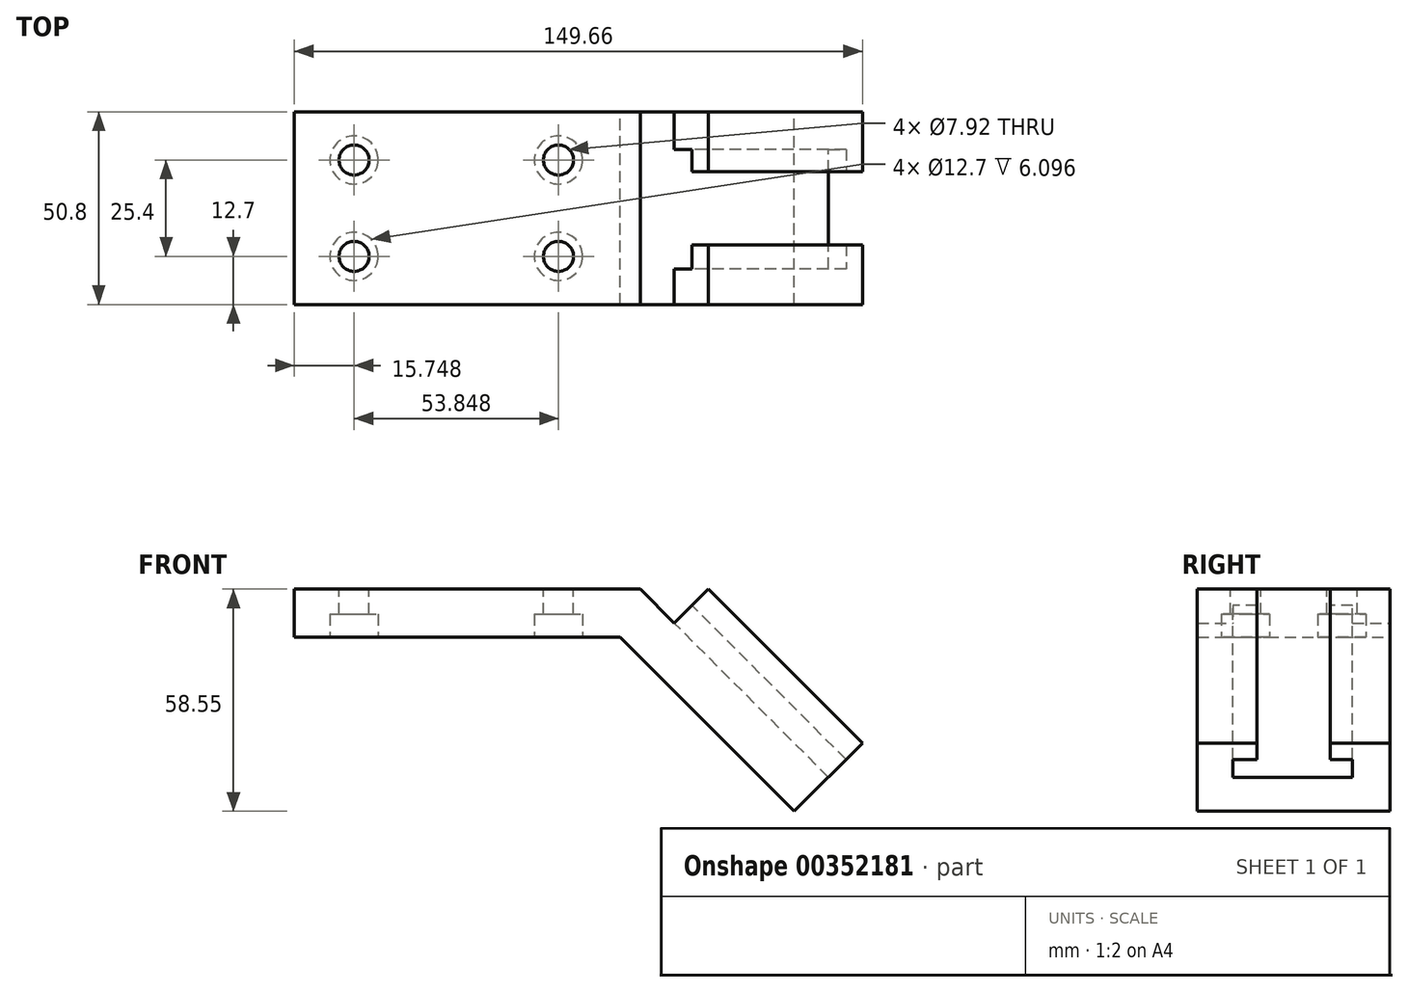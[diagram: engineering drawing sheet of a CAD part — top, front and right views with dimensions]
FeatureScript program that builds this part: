
annotation { "Feature Type Name" : "Feature", "Feature Type Description" : "" }
export const myFeature = defineFeature(function(context is Context, id is Id, definition is map)
    precondition{}
    {
        {
            var Q0;
            Q0=qCreatedBy(makeId("Front.planeOp"),FACE);
            var sketch = newSketch(context, id + "F0", { "sketchPlane" : qUnion([Q0])});
            skLineSegment(sketch, "E0", {"start": v(0, 0) * mm, "end": v(0, -12.7) * mm});
            skLineSegment(sketch, "E1", {"start": v(0, -12.7) * mm, "end": v(85.85, -12.7) * mm});
            skLineSegment(sketch, "E2", {"start": v(0, 0) * mm, "end": v(91.11, 0) * mm});
            skLineSegment(sketch, "E3", {"start": v(91.11, 0) * mm, "end": v(100.1, -8.98) * mm});
            skLineSegment(sketch, "E4", {"start": v(85.85, -12.7) * mm, "end": v(131.7, -58.55) * mm});
            skLineSegment(sketch, "E5", {"start": v(131.7, -58.55) * mm, "end": v(149.66, -40.6) * mm});
            skLineSegment(sketch, "E6", {"start": v(149.66, -40.6) * mm, "end": v(109.07, 0) * mm});
            skLineSegment(sketch, "E7", {"start": v(109.07, 0) * mm, "end": v(100.1, -8.98) * mm});
            skSolve(sketch);
        }
        {
            var Q0;
            Q0 = qSketchRegion(id + "F0", true);
            extrude(context, id + "F1", {"entities" : qUnion([Q0]), "endBound" : BoundingType.SYMMETRIC, "depth" : 50.8 * mm});
        }
        {
            var Q0;
            Q0=makeQuery(id+"F1.opExtrude","SWEPT_FACE",FACE,{"disambiguationData":[OSD([sQuery(id+"F0.wireOp",EDGE,"E2")])]});
            var sketch = newSketch(context, id + "F2", { "sketchPlane" : qUnion([Q0])});
            skCircle(sketch, "E8", {"center": v(15.75, 12.7) * mm, "radius": 3.96 * mm});
            skCircle(sketch, "E9", {"center": v(15.75, -12.7) * mm, "radius": 3.96 * mm});
            skCircle(sketch, "E10", {"center": v(69.6, 12.7) * mm, "radius": 3.96 * mm});
            skCircle(sketch, "E11", {"center": v(69.6, -12.7) * mm, "radius": 3.96 * mm});
            skSolve(sketch);
        }
        {
            var Q0;
            Q0 = qSketchRegion(id + "F2", true);
            extrude(context, id + "F3", {"entities" : qUnion([Q0]), "operationType" : NewBodyOperationType.REMOVE, "endBound" : BoundingType.THROUGH_ALL, "oppositeDirection" : true, "depth" : 25.4 * mm});
        }
        {
            var Q0;
            Q0=makeQuery(id+"F1.opExtrude","SWEPT_FACE",FACE,{"disambiguationData":[OSD([sQuery(id+"F0.wireOp",EDGE,"E1")])]});
            var sketch = newSketch(context, id + "F4", { "sketchPlane" : qUnion([Q0])});
            skCircle(sketch, "E12", {"center": v(15.75, 12.7) * mm, "radius": 6.35 * mm});
            skCircle(sketch, "E13", {"center": v(15.75, -12.7) * mm, "radius": 6.35 * mm});
            skCircle(sketch, "E14", {"center": v(69.6, -12.7) * mm, "radius": 6.35 * mm});
            skCircle(sketch, "E15", {"center": v(69.6, 12.7) * mm, "radius": 6.35 * mm});
            skSolve(sketch);
        }
        {
            var Q0;
            Q0 = qSketchRegion(id + "F4", true);
            extrude(context, id + "F5", {"entities" : qUnion([Q0]), "operationType" : NewBodyOperationType.REMOVE, "oppositeDirection" : true, "depth" : 6.1 * mm});
        }
        {
            var Q0;
            Q0=makeQuery(id+"F1.opExtrude","SWEPT_FACE",FACE,{"disambiguationData":[OSD([sQuery(id+"F0.wireOp",EDGE,"E6")])]});
            var sketch = newSketch(context, id + "F6", { "sketchPlane" : qUnion([Q0])});
            skArc(sketch, "E16", {"start": v(124.49, -25.4) * mm, "mid": v(130.97, -0.03) * mm, "end": v(124.73, 25.4) * mm});
            skLineSegment(sketch, "E17", {"start": v(124.49, -25.4) * mm, "end": v(134.53, -25.4) * mm});
            skLineSegment(sketch, "E18", {"start": v(134.53, -25.4) * mm, "end": v(134.53, 25.4) * mm});
            skLineSegment(sketch, "E19", {"start": v(134.53, 25.4) * mm, "end": v(124.73, 25.4) * mm});
            skSolve(sketch);
        }
        {
            var Q0;
            Q0 = qSketchRegion(id + "F6", true);
            extrude(context, id + "F7", {"entities" : qUnion([Q0]), "operationType" : NewBodyOperationType.ADD, "oppositeDirection" : true, "depth" : 25.4 * mm});
        }
        {
            var Q0;
            Q0 = qSketchRegion(id + "F6", true);
            extrude(context, id + "F8", {"entities" : qUnion([Q0]), "operationType" : NewBodyOperationType.REMOVE, "oppositeDirection" : true, "depth" : 25.4 * mm});
        }
        {
            var Q0;
            Q0=makeQuery(id+"F1.opExtrude","SWEPT_FACE",FACE,{"disambiguationData":[OSD([sQuery(id+"F0.wireOp",EDGE,"E7")])]});
            var sketch = newSketch(context, id + "F9", { "sketchPlane" : qUnion([Q0])});
            skLineSegment(sketch, "E20", {"start": v(9.65, 77.13) * mm, "end": v(9.65, 71.03) * mm});
            skLineSegment(sketch, "E21", {"start": v(9.65, 71.03) * mm, "end": v(16.01, 71.03) * mm});
            skLineSegment(sketch, "E22", {"start": v(16.01, 71.03) * mm, "end": v(16.01, 64.43) * mm});
            skLineSegment(sketch, "E23", {"start": v(16.01, 64.43) * mm, "end": v(-15.48, 64.43) * mm});
            skLineSegment(sketch, "E24", {"start": v(-15.48, 64.43) * mm, "end": v(-15.48, 71.03) * mm});
            skLineSegment(sketch, "E25", {"start": v(-15.48, 71.03) * mm, "end": v(-9.65, 71.03) * mm});
            skLineSegment(sketch, "E26", {"start": v(-9.65, 71.03) * mm, "end": v(-9.65, 77.13) * mm});
            skLineSegment(sketch, "E27", {"start": v(-9.65, 77.13) * mm, "end": v(9.65, 77.13) * mm});
            skSolve(sketch);
        }
        {
            var Q0;
            Q0 = qSketchRegion(id + "F9", true);
            extrude(context, id + "F10", {"entities" : qUnion([Q0]), "operationType" : NewBodyOperationType.REMOVE, "endBound" : BoundingType.THROUGH_ALL, "oppositeDirection" : true, "depth" : 25.4 * mm});
        }
    });
